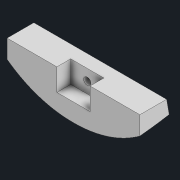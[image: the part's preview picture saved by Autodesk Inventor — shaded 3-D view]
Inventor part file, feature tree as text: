
AUTODESK INVENTOR PART (.ipt)
format: ipt  version: 2022 (Build 260153000, 153)  size: 152,064 bytes
history: native  units: mm
features: sketch x7, extrude x5, projected_geometry x3, revolve x1, hole x1
ambient origin geometry x8: Origin, YZ Plane, XZ Plane, XY Plane, X Axis, Y Axis, Z Axis, Center Point
bodies: Body1 (feature_tree)
feature tree (17):
  revolve  "回転2"
  extrude  "押し出し1"  Depth=120.0mm
  extrude  "押し出し2"  Depth=18.0mm
  extrude  "押し出し3"  Depth=37.5mm
  hole  "穴1"  [1 undecoded]
  extrude  "押し出し4"  Depth=15.0mm
  extrude  "押し出し5"  Depth=20.0mm
  sketch  "スケッチ2"
  sketch  "スケッチ3"
  sketch  "スケッチ5"
  projected_geometry  "投影ループ1"
  sketch  "スケッチ7"
  sketch  "スケッチ8"
  sketch  "スケッチ9"
  projected_geometry  "投影ループ2"
  sketch  "スケッチ10"
  projected_geometry  "投影ループ3"
note: 1 required parameter value undecoded (feature->parameter linkage not recoverable at this tier; creation-order binding heuristic only, values carry confidence <= 0.55)
